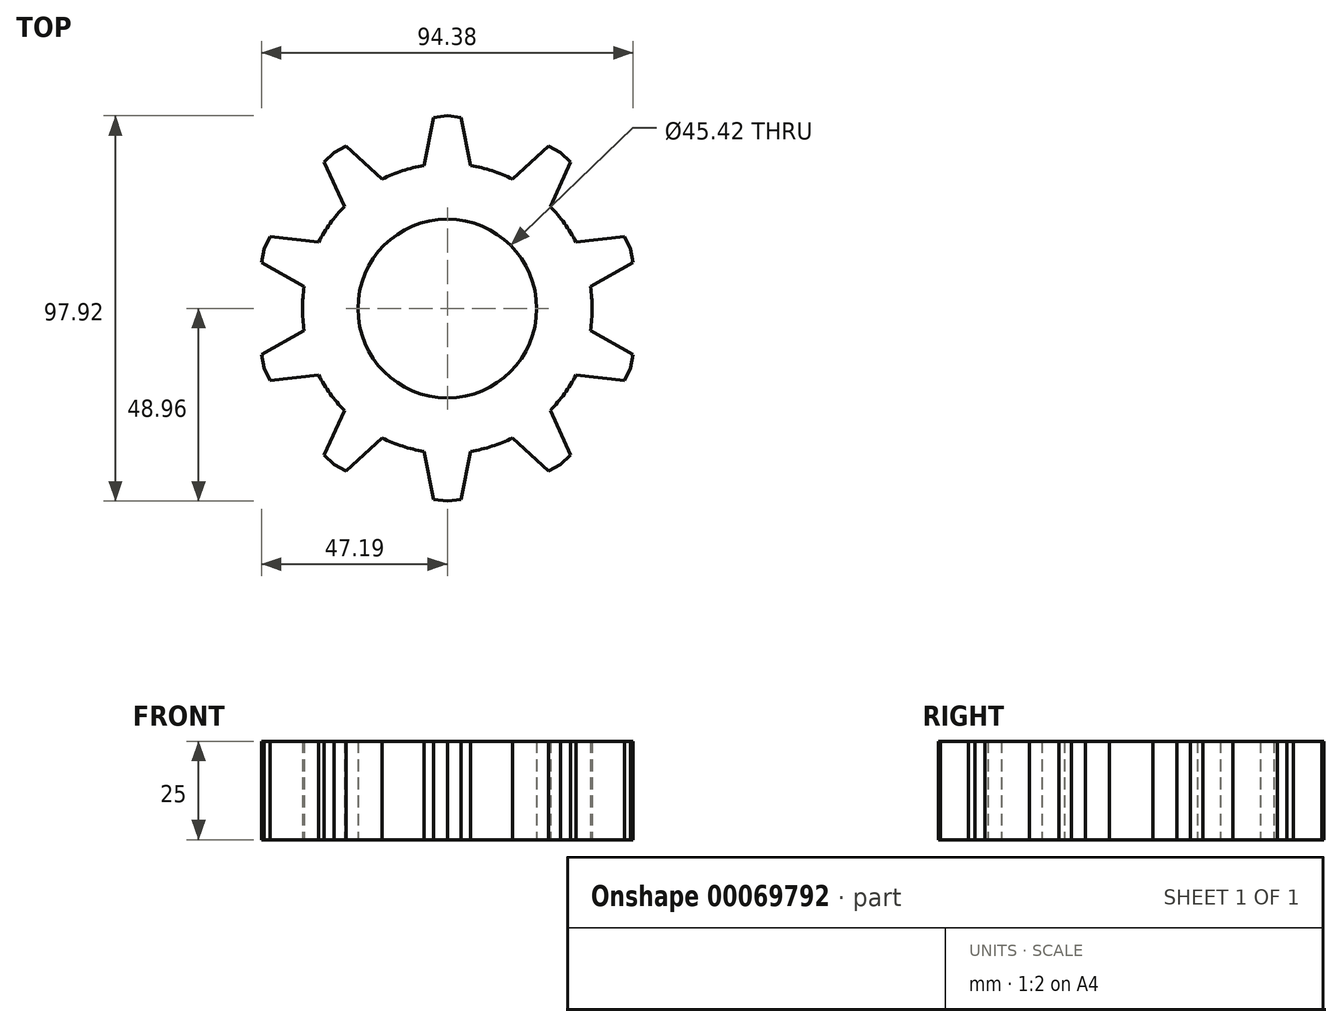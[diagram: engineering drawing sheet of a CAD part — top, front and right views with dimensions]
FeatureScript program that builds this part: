
annotation { "Feature Type Name" : "Feature", "Feature Type Description" : "" }
export const myFeature = defineFeature(function(context is Context, id is Id, definition is map)
    precondition{}
    {
        {
            var Q0;
            Q0=qCreatedBy(makeId("Top.planeOp"),FACE);
            var sketch = newSketch(context, id + "F0", { "sketchPlane" : qUnion([Q0])});
            skLineSegment(sketch, "E0", {"start": v(0, 0) * mm, "end": v(0, 50) * mm});
            skSolve(sketch);
        }
        {
            var Q0;
            Q0=qCreatedBy(makeId("Top.planeOp"),FACE);
            var sketch = newSketch(context, id + "F1", { "sketchPlane" : qUnion([Q0])});
            skLineSegment(sketch, "E1", {"start": v(0, 48.96) * mm, "end": v(3.5, 48.48) * mm});
            skLineSegment(sketch, "E2", {"start": v(3.5, 48.48) * mm, "end": v(5.96, 36.3) * mm});
            skArc(sketch, "E3", {"start": v(-5.96, 36.3) * mm, "mid": v(-11.37, 35) * mm, "end": v(-16.52, 32.87) * mm});
            skLineSegment(sketch, "E4.MirrorCS", {"start": v(-3.5, 48.48) * mm, "end": v(-5.96, 36.3) * mm});
            skLineSegment(sketch, "E5.MirrorCS", {"start": v(0, 48.96) * mm, "end": v(-3.5, 48.48) * mm});
            skLineSegment(sketch, "E6.1.0", {"start": v(-25.67, 41.28) * mm, "end": v(-16.52, 32.87) * mm});
            skLineSegment(sketch, "E6.1.1", {"start": v(-28.78, 39.6) * mm, "end": v(-25.67, 41.28) * mm});
            skLineSegment(sketch, "E6.1.2", {"start": v(-28.78, 39.6) * mm, "end": v(-31.33, 37.17) * mm});
            skLineSegment(sketch, "E6.1.3", {"start": v(-31.33, 37.17) * mm, "end": v(-26.16, 25.87) * mm});
            skLineSegment(sketch, "E6.2.0", {"start": v(-45.03, 18.3) * mm, "end": v(-32.69, 16.88) * mm});
            skLineSegment(sketch, "E6.2.1", {"start": v(-46.56, 15.13) * mm, "end": v(-45.03, 18.3) * mm});
            skLineSegment(sketch, "E6.2.2", {"start": v(-46.56, 15.13) * mm, "end": v(-47.19, 11.65) * mm});
            skLineSegment(sketch, "E6.2.3", {"start": v(-47.19, 11.65) * mm, "end": v(-36.37, 5.55) * mm});
            skLineSegment(sketch, "E6.3.0", {"start": v(-47.19, -11.65) * mm, "end": v(-36.37, -5.55) * mm});
            skLineSegment(sketch, "E6.3.1", {"start": v(-46.56, -15.13) * mm, "end": v(-47.19, -11.65) * mm});
            skLineSegment(sketch, "E6.3.2", {"start": v(-46.56, -15.13) * mm, "end": v(-45.03, -18.3) * mm});
            skLineSegment(sketch, "E6.3.3", {"start": v(-45.03, -18.3) * mm, "end": v(-32.69, -16.88) * mm});
            skLineSegment(sketch, "E6.4.0", {"start": v(-31.33, -37.17) * mm, "end": v(-26.16, -25.87) * mm});
            skLineSegment(sketch, "E6.4.1", {"start": v(-28.78, -39.6) * mm, "end": v(-31.33, -37.17) * mm});
            skLineSegment(sketch, "E6.4.2", {"start": v(-28.78, -39.6) * mm, "end": v(-25.67, -41.28) * mm});
            skLineSegment(sketch, "E6.4.3", {"start": v(-25.67, -41.28) * mm, "end": v(-16.52, -32.87) * mm});
            skLineSegment(sketch, "E6.5.0", {"start": v(-3.5, -48.48) * mm, "end": v(-5.96, -36.3) * mm});
            skLineSegment(sketch, "E6.5.1", {"start": v(0, -48.96) * mm, "end": v(-3.5, -48.48) * mm});
            skLineSegment(sketch, "E6.5.2", {"start": v(0, -48.96) * mm, "end": v(3.5, -48.48) * mm});
            skLineSegment(sketch, "E6.5.3", {"start": v(3.5, -48.48) * mm, "end": v(5.96, -36.3) * mm});
            skLineSegment(sketch, "E6.6.0", {"start": v(25.67, -41.28) * mm, "end": v(16.52, -32.87) * mm});
            skLineSegment(sketch, "E6.6.1", {"start": v(28.78, -39.6) * mm, "end": v(25.67, -41.28) * mm});
            skLineSegment(sketch, "E6.6.2", {"start": v(28.78, -39.6) * mm, "end": v(31.33, -37.17) * mm});
            skLineSegment(sketch, "E6.6.3", {"start": v(31.33, -37.17) * mm, "end": v(26.16, -25.87) * mm});
            skLineSegment(sketch, "E6.7.0", {"start": v(45.03, -18.3) * mm, "end": v(32.69, -16.88) * mm});
            skLineSegment(sketch, "E6.7.1", {"start": v(46.56, -15.13) * mm, "end": v(45.03, -18.3) * mm});
            skLineSegment(sketch, "E6.7.2", {"start": v(46.56, -15.13) * mm, "end": v(47.19, -11.65) * mm});
            skLineSegment(sketch, "E6.7.3", {"start": v(47.19, -11.65) * mm, "end": v(36.37, -5.55) * mm});
            skLineSegment(sketch, "E6.8.0", {"start": v(47.19, 11.65) * mm, "end": v(36.37, 5.55) * mm});
            skLineSegment(sketch, "E6.8.1", {"start": v(46.56, 15.13) * mm, "end": v(47.19, 11.65) * mm});
            skLineSegment(sketch, "E6.8.2", {"start": v(46.56, 15.13) * mm, "end": v(45.03, 18.3) * mm});
            skLineSegment(sketch, "E6.8.3", {"start": v(45.03, 18.3) * mm, "end": v(32.69, 16.88) * mm});
            skLineSegment(sketch, "E6.9.0", {"start": v(31.33, 37.17) * mm, "end": v(26.16, 25.87) * mm});
            skLineSegment(sketch, "E6.9.1", {"start": v(28.78, 39.6) * mm, "end": v(31.33, 37.17) * mm});
            skLineSegment(sketch, "E6.9.2", {"start": v(28.78, 39.6) * mm, "end": v(25.67, 41.28) * mm});
            skLineSegment(sketch, "E6.9.3", {"start": v(25.67, 41.28) * mm, "end": v(16.52, 32.87) * mm});
            skArc(sketch, "E7.trimOffspring", {"start": v(-26.16, 25.87) * mm, "mid": v(-29.77, 21.63) * mm, "end": v(-32.69, 16.88) * mm});
            skArc(sketch, "E8.trimOffspring", {"start": v(-36.37, 5.55) * mm, "mid": v(-36.8, 0) * mm, "end": v(-36.37, -5.55) * mm});
            skArc(sketch, "E9.trimOffspring", {"start": v(-32.69, -16.88) * mm, "mid": v(-29.77, -21.63) * mm, "end": v(-26.16, -25.87) * mm});
            skArc(sketch, "E10.trimOffspring", {"start": v(-16.52, -32.87) * mm, "mid": v(-11.37, -35) * mm, "end": v(-5.96, -36.3) * mm});
            skArc(sketch, "E11.trimOffspring", {"start": v(5.96, -36.3) * mm, "mid": v(11.37, -35) * mm, "end": v(16.52, -32.87) * mm});
            skArc(sketch, "E12.trimOffspring", {"start": v(26.16, -25.87) * mm, "mid": v(29.77, -21.63) * mm, "end": v(32.69, -16.88) * mm});
            skArc(sketch, "E13.trimOffspring", {"start": v(36.37, -5.55) * mm, "mid": v(36.8, 0) * mm, "end": v(36.37, 5.55) * mm});
            skArc(sketch, "E14.trimOffspring", {"start": v(32.69, 16.88) * mm, "mid": v(29.77, 21.63) * mm, "end": v(26.16, 25.87) * mm});
            skArc(sketch, "E15.trimOffspring", {"start": v(16.52, 32.87) * mm, "mid": v(11.37, 35) * mm, "end": v(5.96, 36.3) * mm});
            skCircle(sketch, "E16", {"center": v(0, 0) * mm, "radius": 22.71 * mm});
            skSolve(sketch);
        }
        {
            var Q0;
            Q0=makeQuery(id+"F1.imprint","IMPRINT",FACE,{"disambiguationData":[TD([[makeQuery(id+"F1.imprint","IMPRINT",EDGE,{"derivedFrom":sQuery(id+"F1.wireOp",EDGE,"E1")}),-1.0]])]});
            extrude(context, id + "F2", {"entities" : qUnion([Q0]), "depth" : 25 * mm});
        }
    });
